# Revit family: 307_eb0b83f8372340fea0bac8d04df53b
name_source: partatom
category: Pipe Accessories
units: mm (PartAtom-declared; Revit-internal decimal feet)

## family parameters
Always vertical = Yes
Cut with Voids When Loaded = No
Part Type = Breaks Into
Round Connector Dimension = Use Diameter
Shared = No
Work Plane-Based = No

## types (2) — shared parameters
B = 46 mm  [stored 0.150919 ft]
CenSd_L15_6 = 13 mm
CenSd_L17_6 = 14 mm  [stored 0.0459318 ft]
CenSd_R6_6 = 5 mm  [stored 0.0164042 ft]
Description = SMART swiveling dirt separator with magnetic ins., F-F conn.
L11 = 11 mm  [stored 0.0360892 ft]
L11__ve = -11 mm  [stored -0.0360892 ft]
L12 = 10 mm  [stored 0.0328084 ft]
L12__ve = -10 mm  [stored -0.0328084 ft]
L15 = 15 mm  [stored 0.0492126 ft]
L16 = 8 mm  [stored 0.0262467 ft]
L16__ve = -8 mm  [stored -0.0262467 ft]
L17 = 16 mm  [stored 0.0524934 ft]
L17__ve = -16 mm  [stored -0.0524934 ft]
L22 = 2 mm  [stored 0.00656168 ft]
L22__ve = -2 mm  [stored -0.00656168 ft]
L2D = 102 mm
L2D_Min = 3048 mm
L5 = 5 mm  [stored 0.0164042 ft]
L5__ve = -5 mm  [stored -0.0164042 ft]
L6 = 6 mm  [stored 0.019685 ft]
L6__ve = -6 mm  [stored -0.019685 ft]
LLL = 20 mm  [stored 0.0656168 ft]
LLL__ve = -20 mm  [stored -0.0656168 ft]
Manufacturer = FAR
QmdConnectorList = 301;D;302;D
R12 = 12 mm  [stored 0.0393701 ft]
R6 = 6 mm  [stored 0.019685 ft]
R9 = 9 mm  [stored 0.0295276 ft]
R9__ve = -9 mm  [stored -0.0295276 ft]
W2D = 25 mm  [stored 0.082021 ft]
magiPartTypeId = 307
magiProductFamilyId = eb0b83f8372340fea0bac8d04df53b

## per-type parameters (varying)
| type | AA | AA__ve | CR | CenSd_R3_6 | D | L2 | LL | LNT | LNT__ve | NT | NT__ve | R | R222C | R222S | R3 | R4 | R7 | R71 | R72 | R73 | R75 | magiProductId |
| 2272 1 | 26 mm | -26 mm | 61 mm | 14 mm  [stored 0.0459318 ft] | 25 mm | 51 mm | 13 mm | 82 mm | -82 mm | 10 mm  [stored 0.0328084 ft] | -10 mm  [stored -0.0328084 ft] | 13 mm | 32 mm | 13 mm | 17 mm | 15 mm  [stored 0.0492126 ft] | 29 mm | 28 mm | 31 mm  [stored 0.101706 ft] | 32 mm | 34 mm | 91ba60368024448b924d3748f634a7 |
| 2272 34 | 33 mm  [stored 0.108268 ft] | -33 mm  [stored -0.108268 ft] | 65 mm | 12 mm  [stored 0.0393701 ft] | 20 mm | 44 mm  [stored 0.144357 ft] | 10 mm  [stored 0.0328084 ft] | 70 mm | -70 mm | 9 mm  [stored 0.0295276 ft] | -9 mm  [stored -0.0295276 ft] | 10 mm  [stored 0.0328084 ft] | 28 mm | 12 mm  [stored 0.0393701 ft] | 14 mm  [stored 0.0459318 ft] | 12 mm  [stored 0.0393701 ft] | 25 mm  [stored 0.082021 ft] | 24 mm  [stored 0.0787402 ft] | 27 mm | 28 mm | 30 mm  [stored 0.0984252 ft] | 35f3b2b850e94ac5a021049affc966 |

note: column(s) folded — value = type name in every type: MC Product Code

note: [stored X ft] marks values corroborated as IEEE doubles in the binary element streams (Revit-internal decimal feet)

## geometry (parser evidence)
native form markers: Sweep x2
no freeform markers — native parametric forms only
